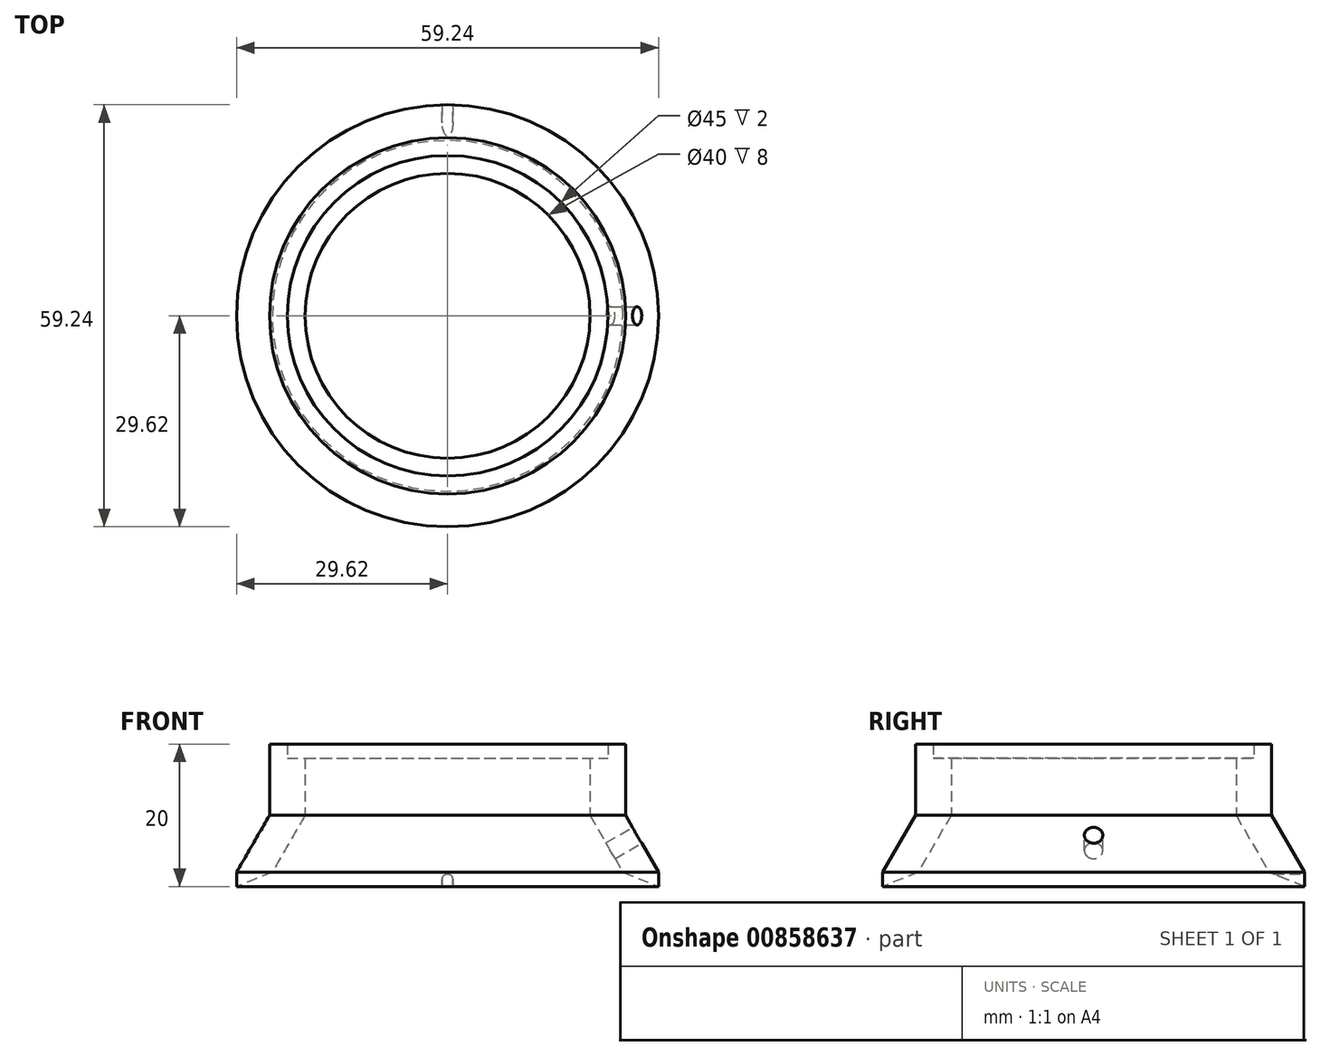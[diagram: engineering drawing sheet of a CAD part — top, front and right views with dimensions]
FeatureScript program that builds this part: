
annotation { "Feature Type Name" : "Feature", "Feature Type Description" : "" }
export const myFeature = defineFeature(function(context is Context, id is Id, definition is map)
    precondition{}
    {
        {
            var Q0;
            Q0=qCreatedBy(makeId("Front.planeOp"),FACE);
            var sketch = newSketch(context, id + "F0", { "sketchPlane" : qUnion([Q0])});
            skLineSegment(sketch, "E0", {"start": v(0, 0) * mm, "end": v(0, 83.69) * mm, "construction": true});
            skLineSegment(sketch, "E1", {"start": v(20, 18) * mm, "end": v(20, 10) * mm});
            skLineSegment(sketch, "E2", {"start": v(20, 10) * mm, "end": v(21.8, 6.87) * mm});
            skLineSegment(sketch, "E3", {"start": v(29.62, 0) * mm, "end": v(29.62, 2) * mm});
            skLineSegment(sketch, "E4", {"start": v(29.62, 2) * mm, "end": v(25, 10) * mm});
            skLineSegment(sketch, "E5", {"start": v(25, 10) * mm, "end": v(25, 18) * mm});
            skLineSegment(sketch, "E6", {"start": v(22.5, 18) * mm, "end": v(20, 18) * mm});
            skLineSegment(sketch, "E7", {"start": v(22.5, 18) * mm, "end": v(22.5, 20) * mm});
            skLineSegment(sketch, "E8", {"start": v(22.5, 20) * mm, "end": v(25, 20) * mm});
            skLineSegment(sketch, "E9", {"start": v(25, 20) * mm, "end": v(25, 18) * mm});
            skLineSegment(sketch, "E10", {"start": v(24.62, 2) * mm, "end": v(29.62, 0) * mm});
            skPoint(sketch, "E11.start.orphan", {"position": v(24.62, 0) * mm});
            skLineSegment(sketch, "E12.trimOffspring", {"start": v(22.3, 6) * mm, "end": v(24.62, 2) * mm});
            skPoint(sketch, "E13", {"position": v(24.52, 6.83) * mm});
            skLineSegment(sketch, "E14", {"start": v(21.8, 6.87) * mm, "end": v(22.3, 6) * mm});
            skSolve(sketch);
        }
        {
            var Q0;
            Q0 = qSketchRegion(id + "F0", true);
            var Q1;
            Q1=sQuery(id+"F0.wireOp",EDGE,"E0");
            revolve(context, id + "F1", {"surfaceOperationType" : NewSurfaceOperationType.NEW, "entities" : qUnion([Q0]), "axis" : qUnion([Q1]), "revolveType" : RevolveType.FULL});
        }
        {
            var Q0;
            Q0=sQuery(id+"F0.wireOp",EDGE,"E4");
            cPlane(context, id + "F2", {"entities" : qUnion([Q0]), "cplaneType" : CPlaneType.LINE_ANGLE, "offset" : 25 * mm, "angle" : 0 * degree, "width" : 150 * mm, "height" : 150 * mm});
        }
        {
            var Q0;
            Q0=qCreatedBy(id+"F2.planeOp",FACE);
            var sketch = newSketch(context, id + "F3", { "sketchPlane" : qUnion([Q0])});
            skPoint(sketch, "E15", {"position": v(0, -7.08) * mm});
            skSolve(sketch);
        }
        {
            var Q0;
            Q0=sQuery(id+"F3.wireOp",VERTEX,"E15");
            var Q1;
            Q1=makeQuery(id+"F1.opRevolve","SWEPT_BODY",BODY,{"disambiguationData":[OSD([sQuery(id+"F0.wireOp",EDGE,"E1"),sQuery(id+"F0.wireOp",EDGE,"E2"),sQuery(id+"F0.wireOp",EDGE,"E3"),sQuery(id+"F0.wireOp",EDGE,"E4"),sQuery(id+"F0.wireOp",EDGE,"E5"),sQuery(id+"F0.wireOp",EDGE,"E6"),sQuery(id+"F0.wireOp",EDGE,"E7"),sQuery(id+"F0.wireOp",EDGE,"E8"),sQuery(id+"F0.wireOp",EDGE,"E9"),sQuery(id+"F0.wireOp",EDGE,"E10"),sQuery(id+"F0.wireOp",EDGE,"E12.trimOffspring"),sQuery(id+"F0.wireOp",EDGE,"E14")])]});
            hole(context, id + "F4", {"style" : HoleStyle.SIMPLE, "endStyle" : HoleEndStyle.THROUGH, "standardTappedOrClearance" : lookupTablePath({ "standard" : "ANSI", "engagement" : "75%", "pitch" : "40 tpi", "size" : "#5", "type" : "Tapped" }), "standardBlindInLast" : lookupTablePath({ "standard" : "ANSI", "engagement" : "75%", "pitch" : "40 tpi", "size" : "#5", "type" : "Tapped" }), "holeDiameter" : 2.58 * mm, "majorDiameter" : 3.17 * mm, "showTappedDepth" : true, "isTappedThrough" : true, "tappedDepth" : 4.05 * mm, "tapClearance" : 3, "locations" : qUnion([Q0]), "scope" : qUnion([Q1])});
        }
        {
            var Q0;
            Q0=qCreatedBy(makeId("Right.planeOp"),FACE);
            var sketch = newSketch(context, id + "F5", { "sketchPlane" : qUnion([Q0])});
            skLineSegment(sketch, "E16", {"start": v(29.62, 0) * mm, "end": v(29.62, 16.97) * mm});
            skSolve(sketch);
        }
        {
            var Q0;
            Q0=sQuery(id+"F5.wireOp",EDGE,"E16");
            cPlane(context, id + "F6", {"entities" : qUnion([Q0]), "cplaneType" : CPlaneType.LINE_ANGLE, "offset" : 25 * mm, "angle" : 90 * degree, "width" : 150 * mm, "height" : 150 * mm});
        }
        {
            var Q0;
            Q0=qCreatedBy(id+"F6.planeOp",FACE);
            var sketch = newSketch(context, id + "F7", { "sketchPlane" : qUnion([Q0])});
            skLineSegment(sketch, "E17.bottom", {"start": v(0.75, 1) * mm, "end": v(-0.75, 1) * mm});
            skLineSegment(sketch, "E17.top", {"start": v(0.75, -1) * mm, "end": v(-0.75, -1) * mm});
            skLineSegment(sketch, "E17.left", {"start": v(0.75, 1) * mm, "end": v(0.75, -1) * mm});
            skLineSegment(sketch, "E17.right", {"start": v(-0.75, 1) * mm, "end": v(-0.75, -1) * mm});
            skPoint(sketch, "E17.middle", {"position": v(0, 0) * mm});
            skArc(sketch, "E18", {"start": v(0.75, 1) * mm, "mid": v(0, 1.75) * mm, "end": v(-0.75, 1) * mm});
            skSolve(sketch);
        }
        {
            var Q0;
            Q0 = qSketchRegion(id + "F7", true);
            extrude(context, id + "F8", {"entities" : qUnion([Q0]), "operationType" : NewBodyOperationType.REMOVE, "oppositeDirection" : true, "depth" : 25 * mm, "offsetDistance" : 25 * mm});
        }
    });
